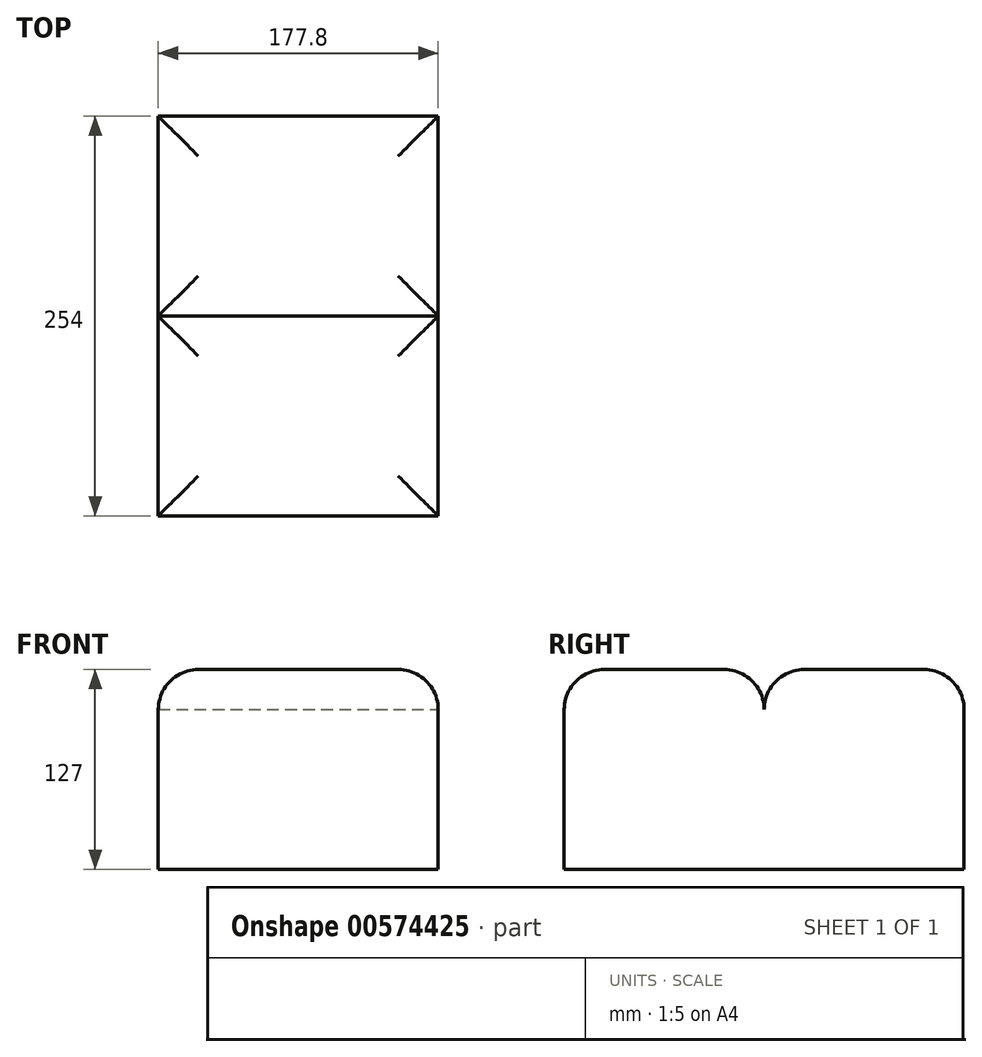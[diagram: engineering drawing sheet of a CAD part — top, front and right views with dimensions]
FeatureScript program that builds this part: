
annotation { "Feature Type Name" : "Feature", "Feature Type Description" : "" }
export const myFeature = defineFeature(function(context is Context, id is Id, definition is map)
    precondition{}
    {
        {
            var Q0;
            Q0=qCreatedBy(makeId("Top.planeOp"),FACE);
            var sketch = newSketch(context, id + "F0", { "sketchPlane" : qUnion([Q0])});
            skLineSegment(sketch, "E0.bottom", {"start": v(0, 0) * mm, "end": v(177.8, 0) * mm});
            skLineSegment(sketch, "E0.top", {"start": v(0, 127) * mm, "end": v(177.8, 127) * mm});
            skLineSegment(sketch, "E0.left", {"start": v(0, 0) * mm, "end": v(0, 127) * mm});
            skLineSegment(sketch, "E0.right", {"start": v(177.8, 0) * mm, "end": v(177.8, 127) * mm});
            skSolve(sketch);
        }
        {
            var Q0;
            Q0 = qSketchRegion(id + "F0", true);
            extrude(context, id + "F1", {"entities" : qUnion([Q0]), "depth" : 127 * mm, "offsetDistance" : 25.4 * mm});
        }
        {
            var Q0;
            Q0=makeQuery(id+"F1.opExtrude","CAP_EDGE",EDGE,{"disambiguationData":[OSD([sQuery(id+"F0.wireOp",EDGE,"E0.left")])],"isStart":false});
            var Q1;
            Q1=makeQuery(id+"F1.opExtrude","CAP_EDGE",EDGE,{"disambiguationData":[OSD([sQuery(id+"F0.wireOp",EDGE,"E0.bottom")])],"isStart":false});
            var Q2;
            Q2=makeQuery(id+"F1.opExtrude","CAP_EDGE",EDGE,{"disambiguationData":[OSD([sQuery(id+"F0.wireOp",EDGE,"E0.top")])],"isStart":false});
            var Q3;
            Q3=makeQuery(id+"F1.opExtrude","CAP_EDGE",EDGE,{"disambiguationData":[OSD([sQuery(id+"F0.wireOp",EDGE,"E0.right")])],"isStart":false});
            fillet(context, id + "F2", {"entities" : qUnion([Q0, Q1, Q2, Q3]), "radius" : 25.4 * mm, "tangentPropagation" : true, "allowEdgeOverflow" : false});
        }
        {
            var Q0;
            Q0=makeQuery(id+"F1.opExtrude","SWEPT_BODY",BODY,{"disambiguationData":[OSD([sQuery(id+"F0.wireOp",EDGE,"E0.bottom"),sQuery(id+"F0.wireOp",EDGE,"E0.top"),sQuery(id+"F0.wireOp",EDGE,"E0.left"),sQuery(id+"F0.wireOp",EDGE,"E0.right")])]});
            var Q1;
            Q1=qCreatedBy(makeId("Front.planeOp"),FACE);
            mirror(context, id + "F3", {"operationType" : NewBodyOperationType.ADD, "entities" : qUnion([Q0]), "mirrorPlane" : qUnion([Q1])});
        }
    });
